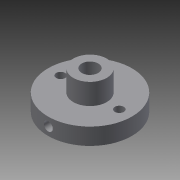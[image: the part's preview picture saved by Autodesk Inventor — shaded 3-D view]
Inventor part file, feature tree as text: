
AUTODESK INVENTOR PART (.ipt)
format: ipt  version: 2013 (Build 170138000, 138)  size: 109,056 bytes
history: native  units: in
note: dims shown in document units (in); Inventor stores cm internally (conversion verified against a paired STEP export)
features: sketch x3, hole x2, revolve x1, plane x1
ambient origin geometry x8: Origin, YZ Plane, XZ Plane, XY Plane, X Axis, Y Axis, Z Axis, Center Point
bodies: Solid1 (feature_tree)
feature tree (7):
  revolve  "Revolution1"  [1 undecoded]
  hole  "Hole1"  [1 undecoded]
  plane  "Work Plane1"
  hole  "Hole2"  [1 undecoded]
  sketch  "Sketch1"  dims[d0=0.0984in d1=0.5in]
  sketch  "Sketch2"  dims[d2=0.2in d3=0.2in]
  sketch  "Sketch3"  dims[d4=0.25in d5=90.0deg d6=0.7in d10=0.1065in d11=0.75in d12=0.375in d13=0.25in d14=0.5635in d15=1.0in d16=0.8108in d17=0.1in d18=0.0in d19=0.1065in d20=0.75in d21=0.375in d22=0.25in d23=0.5635in d24=1.0in d25=0.8108in]
note: 3 required parameter values undecoded (feature->parameter linkage not recoverable at this tier; creation-order binding heuristic only, values carry confidence <= 0.55)